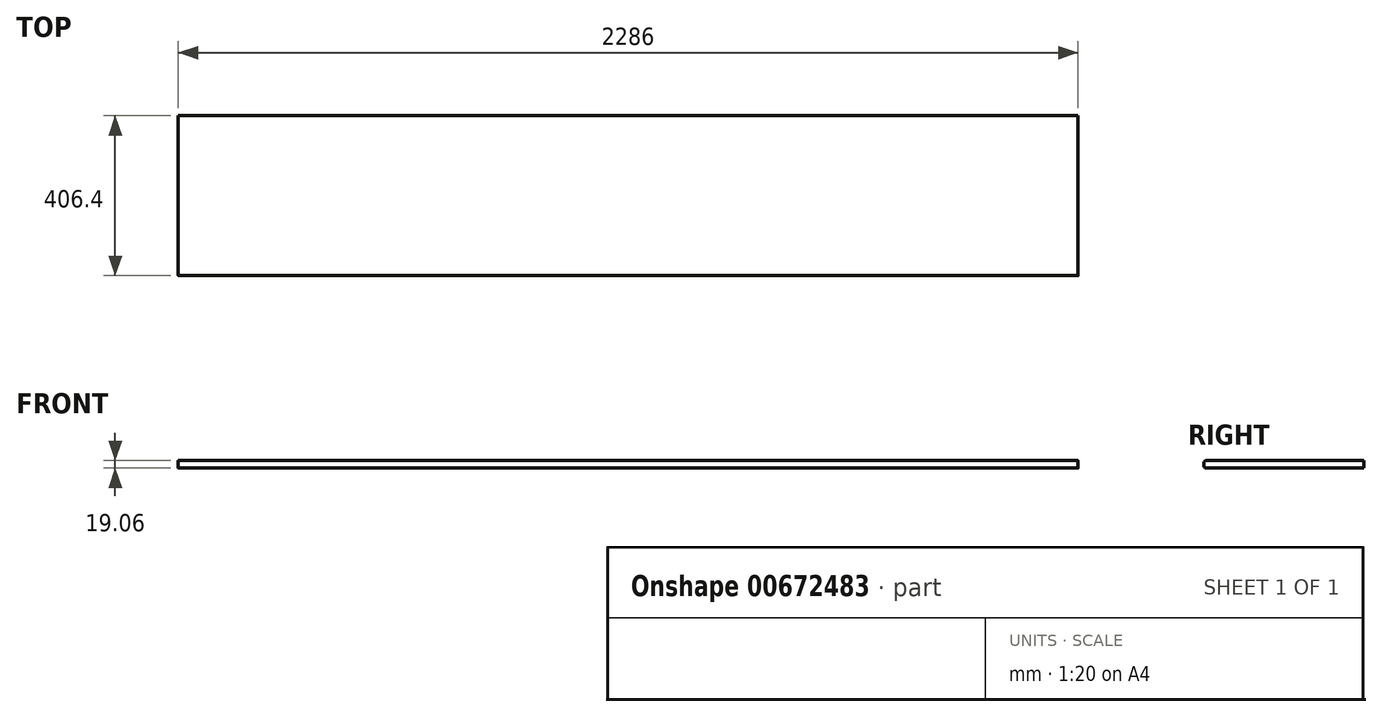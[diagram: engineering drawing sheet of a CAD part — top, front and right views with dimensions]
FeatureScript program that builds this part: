
annotation { "Feature Type Name" : "Feature", "Feature Type Description" : "" }
export const myFeature = defineFeature(function(context is Context, id is Id, definition is map)
    precondition{}
    {
        {
            var Q0;
            Q0=qCreatedBy(makeId("Top.planeOp"),FACE);
            var sketch = newSketch(context, id + "F0", { "sketchPlane" : qUnion([Q0])});
            skLineSegment(sketch, "E0.bottom", {"start": v(-1143, 203.2) * mm, "end": v(1143, 203.2) * mm});
            skLineSegment(sketch, "E0.top", {"start": v(-1143, -203.2) * mm, "end": v(1143, -203.2) * mm});
            skLineSegment(sketch, "E0.left", {"start": v(-1143, 203.2) * mm, "end": v(-1143, -203.2) * mm});
            skLineSegment(sketch, "E0.right", {"start": v(1143, 203.2) * mm, "end": v(1143, -203.2) * mm});
            skSolve(sketch);
        }
        {
            var Q0;
            Q0=makeQuery(id+"F0.imprint","IMPRINT",FACE,{"disambiguationData":[TD([[makeQuery(id+"F0.imprint","IMPRINT",EDGE,{"derivedFrom":sQuery(id+"F0.wireOp",EDGE,"E0.bottom")}),-1.0]])]});
            extrude(context, id + "F1", {"entities" : qUnion([Q0]), "depth" : 9.52 * mm, "offsetDistance" : 25.4 * mm, "hasSecondDirection" : true, "secondDirectionOppositeDirection" : true, "secondDirectionDepth" : 9.52 * mm});
        }
        {
            var Q0;
            Q0=makeQuery(id+"F1.opExtrude","CAP_EDGE",EDGE,{"disambiguationData":[OSD([sQuery(id+"F0.wireOp",EDGE,"E0.top")])],"isStart":false});
            var Q1;
            Q1=makeQuery(id+"F1.opExtrude","CAP_EDGE",EDGE,{"disambiguationData":[OSD([sQuery(id+"F0.wireOp",EDGE,"E0.top")])],"isStart":true});
            fillet(context, id + "F2", {"entities" : qUnion([Q0, Q1]), "radius" : 5.08 * mm, "tangentPropagation" : true, "allowEdgeOverflow" : false});
        }
    });
